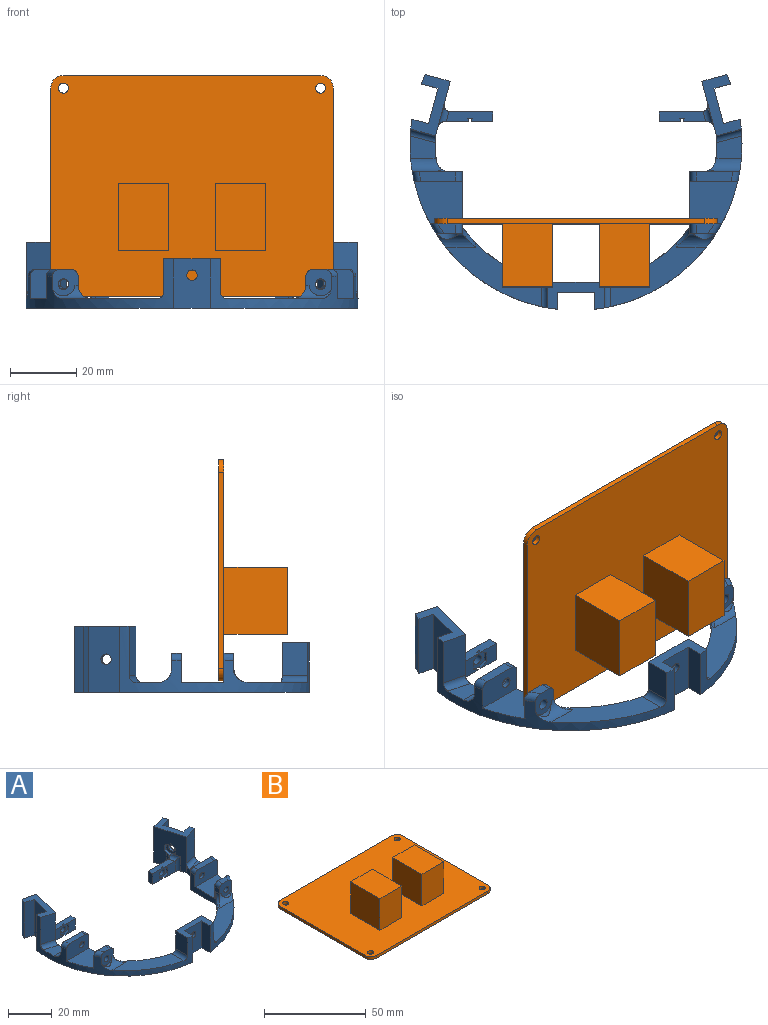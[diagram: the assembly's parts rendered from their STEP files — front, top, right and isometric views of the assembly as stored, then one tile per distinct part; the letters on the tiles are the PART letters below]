
ASSEMBLY  parts=2 mates=1
PART A: 148 faces, bbox 100.8x70.8x20.1 mm
  f0: plane 17x15mm, normal (0,1,0), area 227.6mm2, adj f1,f2,f28,f39,f41,f95,f96,f97
  f1: plane 10x7.77mm, normal (-1,0,0), area 77.7mm2, adj f0,f3,f127,f147
  f2: plane 10x7.77mm, normal (1,0,0), area 77.7mm2, adj f0,f4,f129,f147
  f3: cylinder r=50mm len=57.25mm, axis (0,0,-1), area 383.3mm2, adj f1,f5,f10,f27,f28,f29,f30,f35
  f4: cylinder r=50mm len=57.25mm, axis (0,0,-1), area 383.3mm2, adj f2,f7,f11,f23,f24,f28,f42,f43
  f5: plane 15x5.2mm, normal (1,0,0), area 77.9mm2, adj f3,f6,f28,f147
  f6: plane 15x11mm, normal (0,-1,0), area 157mm2, adj f5,f7,f22,f28,f147
  f7: plane 15x5.2mm, normal (-1,0,0), area 77.9mm2, adj f4,f6,f28,f147
  f8: cylinder r=1.6mm len=3.2mm, axis (0,1,0), area 30.2mm2, adj f43,f58
  f9: cylinder r=1.6mm len=3.2mm, axis (0,1,0), area 30.2mm2, adj f38,f60
  f10: cylinder r=4mm len=11.73mm, axis (1,0,0), area 33mm2, adj f3,f40,f60,f77,f146
  f11: cylinder r=4mm len=11.73mm, axis (1,0,0), area 33mm2, adj f4,f42,f43,f78,f145
  f12: plane 6.57x6mm, normal (0,-1,0), area 28.4mm2, adj f13,f28,f116,f132,f133,f134
  f13: plane 14.07x3.07mm, normal (0,0,1), area 40.2mm2, adj f12,f116,f117,f118,f124,f125,f134,f135
  f14: plane 7.18x6.07mm, normal (0,-1,0), area 32mm2, adj f16,f28,f122,f123,f138,f139,f140
  f15: plane 6.57x6mm, normal (0,-1,0), area 28.4mm2, adj f16,f28,f120,f141,f142,f143
  f16: plane 14.07x3.07mm, normal (0,0,1), area 40.2mm2, adj f14,f15,f119,f120,f121,f122,f140,f141
  f17: cylinder r=1.6mm len=3.2mm, axis (0,-1,0), area 20.1mm2, adj f119,f144
  f18: cylinder r=1.6mm len=3.2mm, axis (0,-1,0), area 20.1mm2, adj f117,f137
  f19: plane 20x16.42mm, normal (0.97,-0.26,0), area 257.2mm2, adj f26,f28,f29,f31,f35,f102,f103,f104
  f20: cylinder r=1.6mm len=3.48mm, axis (-0.97,-0.26,0), area 15.1mm2, adj f55,f115
  f21: cylinder r=1.6mm len=3.48mm, axis (0.97,-0.26,0), area 15.1mm2, adj f34,f108
  f22: cylinder r=1.6mm len=3.2mm, axis (0,1,0), area 15.1mm2, adj f6,f101
  f23: plane 15.18x11.9mm, normal (0,1,0), area 76.9mm2, adj f4,f24,f25,f28,f44,f57,f73,f74
  f24: cylinder r=4mm len=9.61mm, axis (-1,0,0), area 51.3mm2, adj f4,f23,f25,f47,f48,f88,f93
  f25: cylinder r=4mm len=4.92mm, axis (0,0,-1), area 23.3mm2, adj f23,f24,f28,f47,f88,f89
  f26: cylinder r=42.36mm len=7.17mm, axis (0,0,-1), area 22.4mm2, adj f19,f27,f28,f79,f80,f130
  f27: plane 7.85x6.71mm, normal (0,0,1), area 43.6mm2, adj f3,f26,f79,f130
  f28: plane 100x70.66mm, normal (0,0,-1), area 1521.6mm2, adj f0,f3,f4,f5,f6,f7,f12,f14
  f29: plane 15x7.51mm, normal (-0.26,-0.97,0), area 116.6mm2, adj f3,f19,f35,f130
  f30: plane 20x5.02mm, normal (0.26,0.97,0), area 103.9mm2, adj f3,f28,f34,f35
  f31: plane 20x7.51mm, normal (0.26,0.97,0), area 155.4mm2, adj f19,f28,f32,f35
  f32: cylinder r=50mm len=20mm, axis (0,0,-1), area 60.6mm2, adj f28,f31,f33,f35
  f33: plane 20x5.02mm, normal (-0.26,-0.97,0), area 103.9mm2, adj f28,f32,f34,f35
  f34: plane 20x10.63mm, normal (-0.97,0.26,0), area 212mm2, adj f21,f28,f30,f33,f35
  f35: plane 18.43x11.91mm, normal (0,0,1), area 81mm2, adj f3,f19,f29,f30,f31,f32,f33,f34
  f36: plane 18.8x9.76mm, normal (1,0,0), area 77.4mm2, adj f28,f37,f38,f60,f62,f63,f68,f69
  f37: plane 14.44x12.8mm, normal (0,0,1), area 158mm2, adj f3,f36,f38,f62
  f38: plane 9.57x8.76mm, normal (0,1,0), area 73.9mm2, adj f3,f9,f36,f37,f61,f67,f68
  f39: cylinder r=42.36mm len=25.39mm, axis (0,0,-1), area 96.7mm2, adj f0,f28,f40,f75,f77,f127
  f40: plane 28.73x19.27mm, normal (0,0,1), area 214.2mm2, adj f3,f10,f39,f77,f127
  f41: cylinder r=42.36mm len=25.39mm, axis (0,0,-1), area 96.7mm2, adj f0,f28,f42,f76,f78,f129
  f42: plane 28.73x19.27mm, normal (0,0,1), area 214.2mm2, adj f4,f11,f41,f78,f129
  f43: plane 7.95x7.79mm, normal (0,-1,0), area 44.2mm2, adj f4,f8,f11,f44,f59,f71,f72,f145
  f44: plane 18.8x9.76mm, normal (-1,0,0), area 77.4mm2, adj f23,f28,f43,f45,f46,f58,f71,f73
  f45: plane 14.44x12.8mm, normal (0,0,1), area 158mm2, adj f4,f44,f46,f58
  f46: plane 14.44x8.76mm, normal (0,-1,0), area 116.6mm2, adj f4,f44,f45,f57,f66,f73,f74
  f47: cylinder r=42.36mm len=7.17mm, axis (0,0,-1), area 22.4mm2, adj f24,f25,f28,f48,f53,f128
  f48: plane 7.85x6.71mm, normal (0,0,1), area 43.6mm2, adj f4,f24,f47,f128
  f49: plane 15x7.51mm, normal (0.26,-0.97,0), area 116.6mm2, adj f4,f53,f56,f128
  f50: plane 20x5.02mm, normal (0.26,-0.97,0), area 103.9mm2, adj f28,f51,f55,f56
  f51: cylinder r=50mm len=20mm, axis (0,0,-1), area 60.6mm2, adj f28,f50,f52,f56
  f52: plane 20x7.51mm, normal (-0.26,0.97,0), area 155.4mm2, adj f28,f51,f53,f56
  f53: plane 20x16.42mm, normal (-0.97,-0.26,0), area 257.2mm2, adj f28,f47,f49,f52,f56,f109,f110,f111
  f54: plane 20x5.02mm, normal (-0.26,0.97,0), area 103.9mm2, adj f4,f28,f55,f56
  f55: plane 20x10.63mm, normal (0.97,0.26,0), area 212mm2, adj f20,f28,f50,f54,f56
  f56: plane 18.43x11.91mm, normal (0,0,1), area 81mm2, adj f4,f49,f50,f51,f52,f53,f54,f55
  f57: plane 11x3mm, normal (0,0,1), area 32.1mm2, adj f23,f46,f73,f74
  f58: plane 9.57x8.76mm, normal (0,1,0), area 73.9mm2, adj f4,f8,f44,f45,f59,f71,f72
  f59: plane 5.28x3mm, normal (0,0,1), area 13.1mm2, adj f43,f58,f71,f72
  f60: plane 7.95x7.79mm, normal (0,-1,0), area 44.1mm2, adj f3,f9,f10,f36,f61,f67,f68,f146
  f61: plane 5.28x3mm, normal (0,0,1), area 13.1mm2, adj f38,f60,f67,f68
  f62: plane 14.44x8.76mm, normal (0,-1,0), area 116.6mm2, adj f3,f36,f37,f64,f65,f69,f70
  f63: plane 15.18x11.9mm, normal (0,1,0), area 76.9mm2, adj f3,f28,f36,f64,f69,f70,f79,f80
  f64: plane 11x3mm, normal (0,0,1), area 32.1mm2, adj f62,f63,f69,f70
  f65: cylinder r=1.6mm len=3.2mm, axis (0,1,0), area 15.1mm2, adj f62,f87
  f66: cylinder r=1.6mm len=3.2mm, axis (0,1,0), area 15.1mm2, adj f46,f94
  f67: torus R=48mm, axis (0,0,1), area 11mm2, adj f3,f38,f60,f61
  f68: cylinder r=2mm len=3mm, axis (0,-1,0), area 9.4mm2, adj f36,f38,f60,f61
  f69: cylinder r=2mm len=3mm, axis (0,-1,0), area 9.4mm2, adj f36,f62,f63,f64
  f70: torus R=48mm, axis (0,0,1), area 9.5mm2, adj f3,f62,f63,f64
  f71: cylinder r=2mm len=3mm, axis (0,1,0), area 9.4mm2, adj f43,f44,f58,f59
  f72: torus R=48mm, axis (0,0,1), area 11mm2, adj f4,f43,f58,f59
  f73: cylinder r=2mm len=3mm, axis (0,1,0), area 9.4mm2, adj f23,f44,f46,f57
  f74: torus R=48mm, axis (0,0,1), area 9.5mm2, adj f4,f23,f46,f57
  f75: cylinder r=2mm len=7mm, axis (0,0,-1), area 7.9mm2, adj f28,f36,f39,f77
  f76: cylinder r=2mm len=7mm, axis (0,0,-1), area 7.9mm2, adj f28,f41,f44,f78
  f77: cylinder r=4mm len=6.78mm, axis (0,1,0), area 11.5mm2, adj f10,f36,f39,f40,f75
  f78: cylinder r=4mm len=6.78mm, axis (0,-1,0), area 11.5mm2, adj f11,f41,f42,f44,f76
  f79: cylinder r=4mm len=9.61mm, axis (-1,0,0), area 51.3mm2, adj f3,f26,f27,f63,f80,f84,f86
  f80: cylinder r=4mm len=4.92mm, axis (0,0,-1), area 23.3mm2, adj f26,f28,f63,f79,f85,f86
  f81: plane 2.81x1.63mm, normal (-0.5,0,-0.87), area 4.9mm2, adj f63,f82,f83,f87
  f82: plane 3.25x1.5mm, normal (-1,0,0), area 4.9mm2, adj f63,f81,f85,f87
  f83: plane 2.81x1.63mm, normal (0.5,0,-0.87), area 4.9mm2, adj f63,f81,f84,f87
  f84: plane 3.25x1.72mm, normal (1,0,0), area 5mm2, adj f63,f79,f83,f86,f87
  f85: plane 2.82x1.63mm, normal (-0.5,0,0.87), area 4.9mm2, adj f63,f80,f82,f86,f87
  f86: plane 2.85x2.12mm, normal (0.5,0,0.87), area 5.9mm2, adj f79,f80,f84,f85,f87
  f87: plane 6.5x5.63mm, normal (0,1,0), area 19.4mm2, adj f65,f81,f82,f83,f84,f85,f86
  f88: plane 2.85x2.12mm, normal (-0.5,0,0.87), area 5.9mm2, adj f24,f25,f89,f93,f94
  f89: plane 2.82x1.63mm, normal (0.5,0,0.87), area 4.9mm2, adj f23,f25,f88,f90,f94
  f90: plane 3.25x1.5mm, normal (1,0,0), area 4.9mm2, adj f23,f89,f91,f94
  f91: plane 2.81x1.63mm, normal (0.5,0,-0.87), area 4.9mm2, adj f23,f90,f92,f94
  f92: plane 2.81x1.63mm, normal (-0.5,0,-0.87), area 4.9mm2, adj f23,f91,f93,f94
  f93: plane 3.25x1.72mm, normal (-1,0,0), area 5mm2, adj f23,f24,f88,f92,f94
  f94: plane 6.5x5.63mm, normal (0,1,0), area 19.4mm2, adj f66,f88,f89,f90,f91,f92,f93
  f95: plane 2.81x1.63mm, normal (0.5,0,-0.87), area 4.9mm2, adj f0,f96,f100,f101
  f96: plane 2.81x1.63mm, normal (-0.5,0,-0.87), area 4.9mm2, adj f0,f95,f97,f101
  f97: plane 3.25x1.5mm, normal (-1,0,0), area 4.9mm2, adj f0,f96,f98,f101
  f98: plane 2.81x1.63mm, normal (-0.5,0,0.87), area 4.9mm2, adj f0,f97,f99,f101
  f99: plane 2.81x1.63mm, normal (0.5,0,0.87), area 4.9mm2, adj f0,f98,f100,f101
  f100: plane 3.25x1.5mm, normal (1,0,0), area 4.9mm2, adj f0,f95,f99,f101
  f101: plane 6.5x5.63mm, normal (0,1,0), area 19.4mm2, adj f22,f95,f96,f97,f98,f99,f100
  f102: plane 3.24x2.73mm, normal (0.13,0.48,0.87), area 5.2mm2, adj f19,f103,f107,f108,f125
  f103: plane 3.26x2.22mm, normal (-0.13,-0.48,0.87), area 5.2mm2, adj f19,f102,f104,f108,f124,f125
  f104: plane 3.25x1.45mm, normal (-0.26,-0.97,0), area 4.9mm2, adj f19,f103,f105,f108
  f105: plane 3.11x2.18mm, normal (-0.13,-0.48,-0.87), area 4.9mm2, adj f19,f104,f106,f108
  f106: plane 3.11x2.18mm, normal (0.13,0.48,-0.87), area 4.9mm2, adj f19,f105,f107,f108
  f107: plane 3.25x1.45mm, normal (0.26,0.97,0), area 4.9mm2, adj f19,f102,f106,f108
  f108: plane 6.5x5.44mm, normal (0.97,-0.26,0), area 19.4mm2, adj f21,f102,f103,f104,f105,f106,f107
  f109: plane 3.24x2.73mm, normal (-0.13,0.48,0.87), area 5.2mm2, adj f53,f110,f114,f115,f122
  f110: plane 3.25x1.45mm, normal (-0.26,0.97,0), area 4.9mm2, adj f53,f109,f111,f115
  f111: plane 3.11x2.18mm, normal (-0.13,0.48,-0.87), area 4.9mm2, adj f53,f110,f112,f115
  f112: plane 3.11x2.18mm, normal (0.13,-0.48,-0.87), area 4.9mm2, adj f53,f111,f113,f115
  f113: plane 3.25x1.45mm, normal (0.26,-0.97,0), area 4.9mm2, adj f53,f112,f114,f115
  f114: plane 3.26x2.22mm, normal (0.13,-0.48,0.87), area 5.2mm2, adj f53,f109,f113,f115,f121,f122
  f115: plane 6.5x5.44mm, normal (-0.97,-0.26,0), area 19.4mm2, adj f20,f109,f110,f111,f112,f113,f114
  f116: plane 6x3mm, normal (1,0,0), area 18mm2, adj f12,f13,f28,f117
  f117: plane 12.73x6mm, normal (0,1,0), area 68.3mm2, adj f13,f18,f28,f116,f124
  f118: plane 7.18x6.07mm, normal (0,-1,0), area 32mm2, adj f13,f28,f125,f126,f131,f135,f136
  f119: plane 12.73x6mm, normal (0,1,0), area 68.3mm2, adj f16,f17,f28,f120,f121
  f120: plane 6x3mm, normal (-1,0,0), area 18mm2, adj f15,f16,f28,f119
  f121: cylinder r=2mm len=7.69mm, axis (0,0,-1), area 24.2mm2, adj f16,f28,f53,f114,f119,f122
  f122: cylinder r=2mm len=6.81mm, axis (0.26,-0.97,0), area 12.1mm2, adj f14,f16,f53,f109,f114,f121,f123
  f123: cylinder r=2mm len=8mm, axis (0,0,-1), area 18mm2, adj f14,f28,f53,f122
  f124: cylinder r=2mm len=7.69mm, axis (0,0,1), area 24.2mm2, adj f13,f19,f28,f103,f117,f125
  f125: cylinder r=2mm len=6.81mm, axis (0.26,0.97,0), area 12.1mm2, adj f13,f19,f102,f103,f118,f124,f126
  f126: cylinder r=2mm len=8mm, axis (0,0,1), area 18mm2, adj f19,f28,f118,f125
  f127: cylinder r=2mm len=8.23mm, axis (0,-1,0), area 24.3mm2, adj f1,f3,f39,f40
  f128: cylinder r=2mm len=8.47mm, axis (0.97,0.26,0), area 24.3mm2, adj f4,f47,f48,f49
  f129: cylinder r=2mm len=8.23mm, axis (0,1,0), area 24.3mm2, adj f2,f4,f41,f42
  f130: cylinder r=2mm len=8.47mm, axis (0.97,-0.26,0), area 24.3mm2, adj f3,f26,f27,f29
  f131: plane 2.38x1.38mm, normal (0.5,0,0.87), area 2.8mm2, adj f28,f118,f136,f137
  f132: plane 2.38x1.38mm, normal (-0.5,0,0.87), area 2.8mm2, adj f12,f28,f133,f137
  f133: plane 3.25x1mm, normal (-1,0,0), area 3.3mm2, adj f12,f132,f134,f137
  f134: plane 2.38x1.38mm, normal (-0.5,0,-0.87), area 2.8mm2, adj f12,f13,f133,f137
  f135: plane 2.38x1.38mm, normal (0.5,0,-0.87), area 2.8mm2, adj f13,f118,f136,f137
  f136: plane 3.25x1mm, normal (1,0,0), area 3.3mm2, adj f118,f131,f135,f137
  f137: plane 6x5.63mm, normal (0,-1,0), area 19.2mm2, adj f13,f18,f28,f131,f132,f133,f134,f135
  f138: plane 2.38x1.38mm, normal (-0.5,0,0.87), area 2.8mm2, adj f14,f28,f139,f144
  f139: plane 3.25x1mm, normal (-1,0,0), area 3.3mm2, adj f14,f138,f140,f144
  f140: plane 2.38x1.38mm, normal (-0.5,0,-0.87), area 2.8mm2, adj f14,f16,f139,f144
  f141: plane 2.38x1.38mm, normal (0.5,0,-0.87), area 2.8mm2, adj f15,f16,f142,f144
  f142: plane 3.25x1mm, normal (1,0,0), area 3.3mm2, adj f15,f141,f143,f144
  f143: plane 2.38x1.38mm, normal (0.5,0,0.87), area 2.8mm2, adj f15,f28,f142,f144
  f144: plane 6x5.63mm, normal (0,-1,0), area 19.2mm2, adj f16,f17,f28,f138,f139,f140,f141,f142
  f145: cylinder r=3.5mm len=6.83mm, axis (0,1,0), area 7.8mm2, adj f4,f11,f43
  f146: cylinder r=3.5mm len=6.83mm, axis (0,1,0), area 7.8mm2, adj f3,f10,f60
  f147: plane 17x8.2mm, normal (0,0,1), area 81mm2, adj f0,f1,f2,f3,f4,f5,f6,f7
PART B: 24 faces, bbox 85.1x66.7x20.6 mm
  f0: plane 85.09x66.68mm, normal (0,0,1), area 5013.3mm2, adj f1,f2,f3,f4,f5,f6,f7,f8
  f1: plane 59.06x1.6mm, normal (1,0,0), area 94.5mm2, adj f0,f2,f12,f13
  f2: cylinder r=3.81mm len=3.81mm, axis (0,0,-1), area 9.6mm2, adj f0,f1,f3,f13
  f3: plane 77.47x1.6mm, normal (0,1,0), area 124mm2, adj f0,f2,f4,f13
  f4: cylinder r=3.81mm len=3.81mm, axis (0,0,-1), area 9.6mm2, adj f0,f3,f5,f13
  f5: plane 59.06x1.6mm, normal (-1,0,0), area 94.5mm2, adj f0,f4,f6,f13
  f6: cylinder r=3.81mm len=3.81mm, axis (0,0,-1), area 9.6mm2, adj f0,f5,f7,f13
  f7: plane 77.47x1.6mm, normal (0,-1,0), area 124mm2, adj f0,f6,f12,f13
  f8: cylinder r=1.5mm len=3mm, axis (0,0,-1), area 15.1mm2, adj f0,f13
  f9: cylinder r=1.5mm len=3mm, axis (0,0,-1), area 15.1mm2, adj f0,f13
  f10: cylinder r=1.5mm len=3mm, axis (0,0,-1), area 15.1mm2, adj f0,f13
  f11: cylinder r=1.5mm len=3mm, axis (0,0,-1), area 15.1mm2, adj f0,f13
  f12: cylinder r=3.81mm len=3.81mm, axis (0,0,-1), area 9.6mm2, adj f0,f1,f7,f13
  f13: plane 85.09x66.68mm, normal (0,0,-1), area 5632.6mm2, adj f1,f2,f3,f4,f5,f6,f7,f8
  f14: plane 20.32x19mm, normal (-1,0,0), area 386.1mm2, adj f0,f15,f17,f18
  f15: plane 19x15.24mm, normal (0,-1,0), area 289.6mm2, adj f0,f14,f16,f18
  f16: plane 20.32x19mm, normal (1,0,0), area 386.1mm2, adj f0,f15,f17,f18
  f17: plane 19x15.24mm, normal (0,1,0), area 289.6mm2, adj f0,f14,f16,f18
  f18: plane 20.32x15.24mm, normal (0,0,1), area 309.7mm2, adj f14,f15,f16,f17
  f19: plane 20.32x19mm, normal (1,0,0), area 386.1mm2, adj f0,f20,f22,f23
  f20: plane 19x15.24mm, normal (0,1,0), area 289.6mm2, adj f0,f19,f21,f23
  f21: plane 20.32x19mm, normal (-1,0,0), area 386.1mm2, adj f0,f20,f22,f23
  f22: plane 19x15.24mm, normal (0,-1,0), area 289.6mm2, adj f0,f19,f21,f23
  f23: plane 20.32x15.24mm, normal (0,0,1), area 309.7mm2, adj f19,f20,f21,f22
PLACE A t=(-803.15,-352.78,-41.06)mm
PLACE B rot(axis=(1,0,0),90deg) t=(-95.69,-75.18,-37.56)mm
MATE fastened B.f10 <-> A.f8  axis (0,-1,0) through (-14.41,-76.78,-33.75)mm
